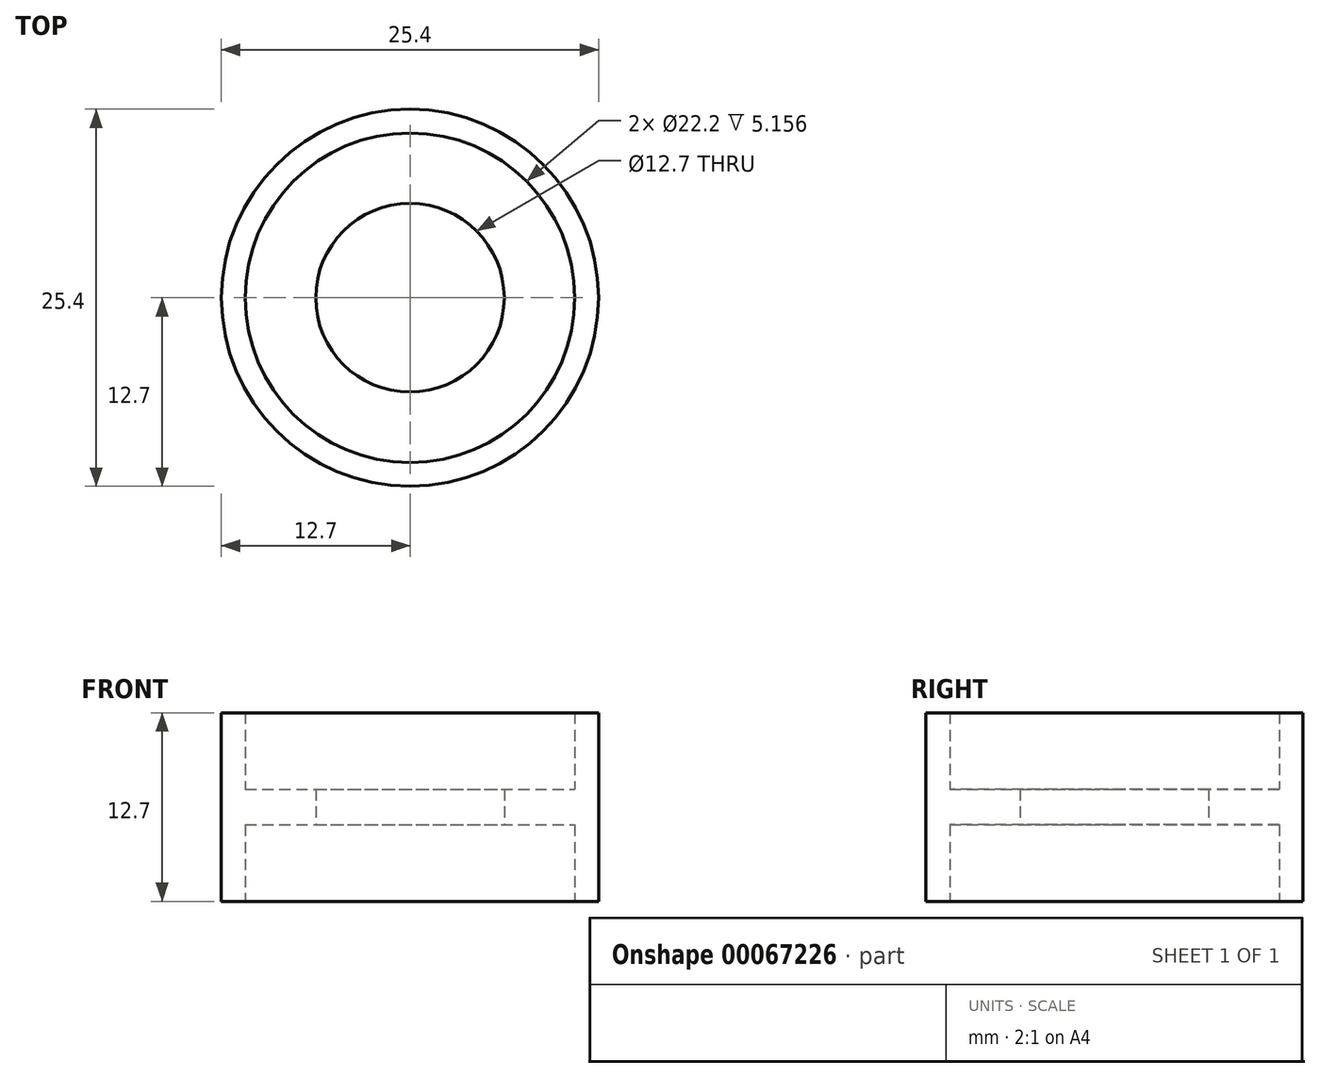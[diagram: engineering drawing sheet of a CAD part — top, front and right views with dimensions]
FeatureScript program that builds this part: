
annotation { "Feature Type Name" : "Feature", "Feature Type Description" : "" }
export const myFeature = defineFeature(function(context is Context, id is Id, definition is map)
    precondition{}
    {
        {
            var Q0;
            Q0=qCreatedBy(makeId("Front.planeOp"),FACE);
            var sketch = newSketch(context, id + "F0", { "sketchPlane" : qUnion([Q0])});
            skLineSegment(sketch, "E0", {"start": v(0, 0) * mm, "end": v(0, 24.12) * mm, "construction": true});
            skLineSegment(sketch, "E1", {"start": v(11.1, 0) * mm, "end": v(11.1, 5.16) * mm});
            skLineSegment(sketch, "E2", {"start": v(11.1, 5.16) * mm, "end": v(6.35, 5.16) * mm});
            skLineSegment(sketch, "E3", {"start": v(6.35, 5.16) * mm, "end": v(6.35, 7.54) * mm});
            skLineSegment(sketch, "E4", {"start": v(6.35, 7.54) * mm, "end": v(11.1, 7.54) * mm});
            skLineSegment(sketch, "E5", {"start": v(11.1, 7.54) * mm, "end": v(11.1, 12.7) * mm});
            skLineSegment(sketch, "E6", {"start": v(11.1, 12.7) * mm, "end": v(12.7, 12.7) * mm});
            skLineSegment(sketch, "E7", {"start": v(12.7, 12.7) * mm, "end": v(12.7, 0) * mm});
            skLineSegment(sketch, "E8", {"start": v(12.7, 0) * mm, "end": v(11.1, 0) * mm});
            skSolve(sketch);
        }
        {
            var Q0;
            Q0=makeQuery(id+"F0.imprint","IMPRINT",FACE,{"disambiguationData":[TD([[makeQuery(id+"F0.imprint","IMPRINT",EDGE,{"derivedFrom":sQuery(id+"F0.wireOp",EDGE,"E1")}),-1.0]])]});
            var Q1;
            Q1 = qSketchRegion(id + "F0", true);
            var Q2;
            Q2=sQuery(id+"F0.wireOp",EDGE,"E0");
            revolve(context, id + "F1", {"entities" : qUnion([Q0, Q1]), "axis" : qUnion([Q2]), "revolveType" : RevolveType.FULL});
        }
    });
